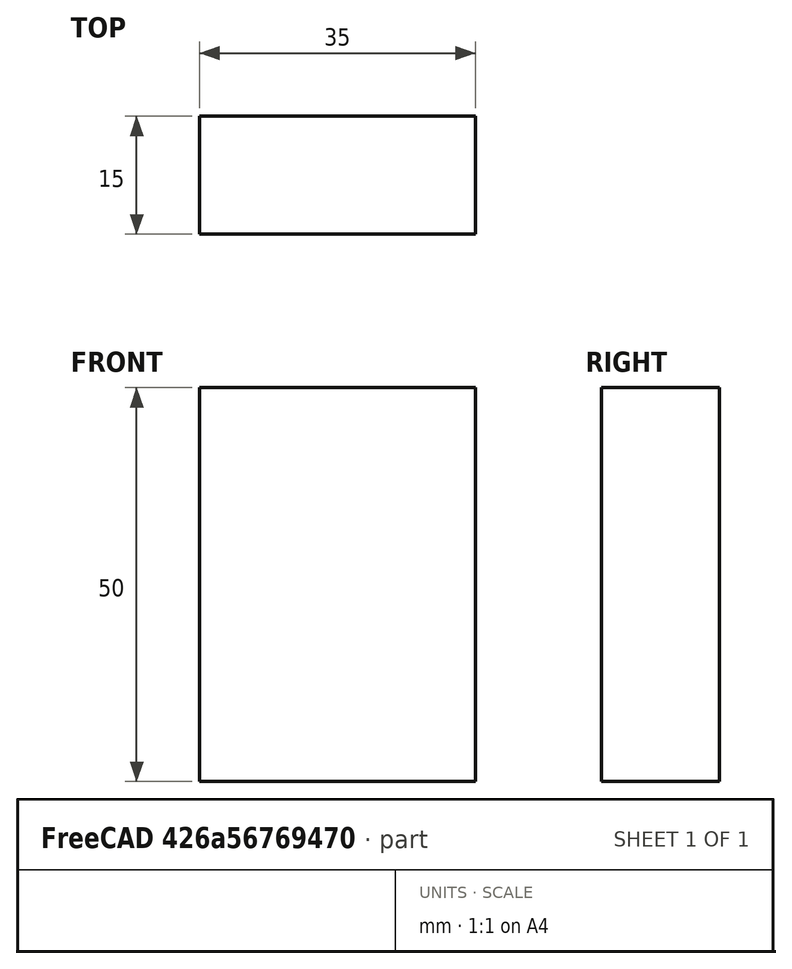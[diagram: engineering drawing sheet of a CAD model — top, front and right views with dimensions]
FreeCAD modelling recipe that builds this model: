
FCSTD DOCUMENT  (FreeCAD 0.15R4671 (Git))
Label: Flat Bar 35x15 EN10058 S235JR
License: All rights reserved
LicenseURL: http://en.wikipedia.org/wiki/All_rights_reserved
objects: Sketcher::SketchObject×1, Part::Extrusion×1
note: 2 computed .brp shape members not serialized (recipe doc carries the construction recipe); baked Part::Feature solids carry a one-line shape summary decoded from their .brp

FEATURE [Sketcher::SketchObject] Sketch
  sketch-geometry (4):
    g0: LineSegment StartX=-17.5 StartY=-7.5 StartZ=0 EndX=17.5 EndY=-7.5 EndZ=0
    g1: LineSegment StartX=17.5 StartY=-7.5 StartZ=0 EndX=17.5 EndY=7.5 EndZ=0
    g2: LineSegment StartX=17.5 StartY=7.5 StartZ=0 EndX=-17.5 EndY=7.5 EndZ=0
    g3: LineSegment StartX=-17.5 StartY=7.5 StartZ=0 EndX=-17.5 EndY=-7.5 EndZ=0
  constraints (12):
    c: Coincident(g0,g1)
    c: Coincident(g1,g2)
    c: Coincident(g2,g3)
    c: Coincident(g3,g0)
    c: Horizontal(g0)
    c: Horizontal(g2)
    c: Vertical(g1)
    c: Vertical(g3)
    c: Symmetric(g1,g2,g-2)
    c: Symmetric(g0,g1,g-1)
    c: DistanceY(g1) = 15
    c: DistanceX(g0) = 35
FEATURE [Part::Extrusion] Extrude  label="Flat Bar 35x15 EN10058 S235JR"
  Base = -> Sketch
  Dir = (0,0,50)
  Solid = true
